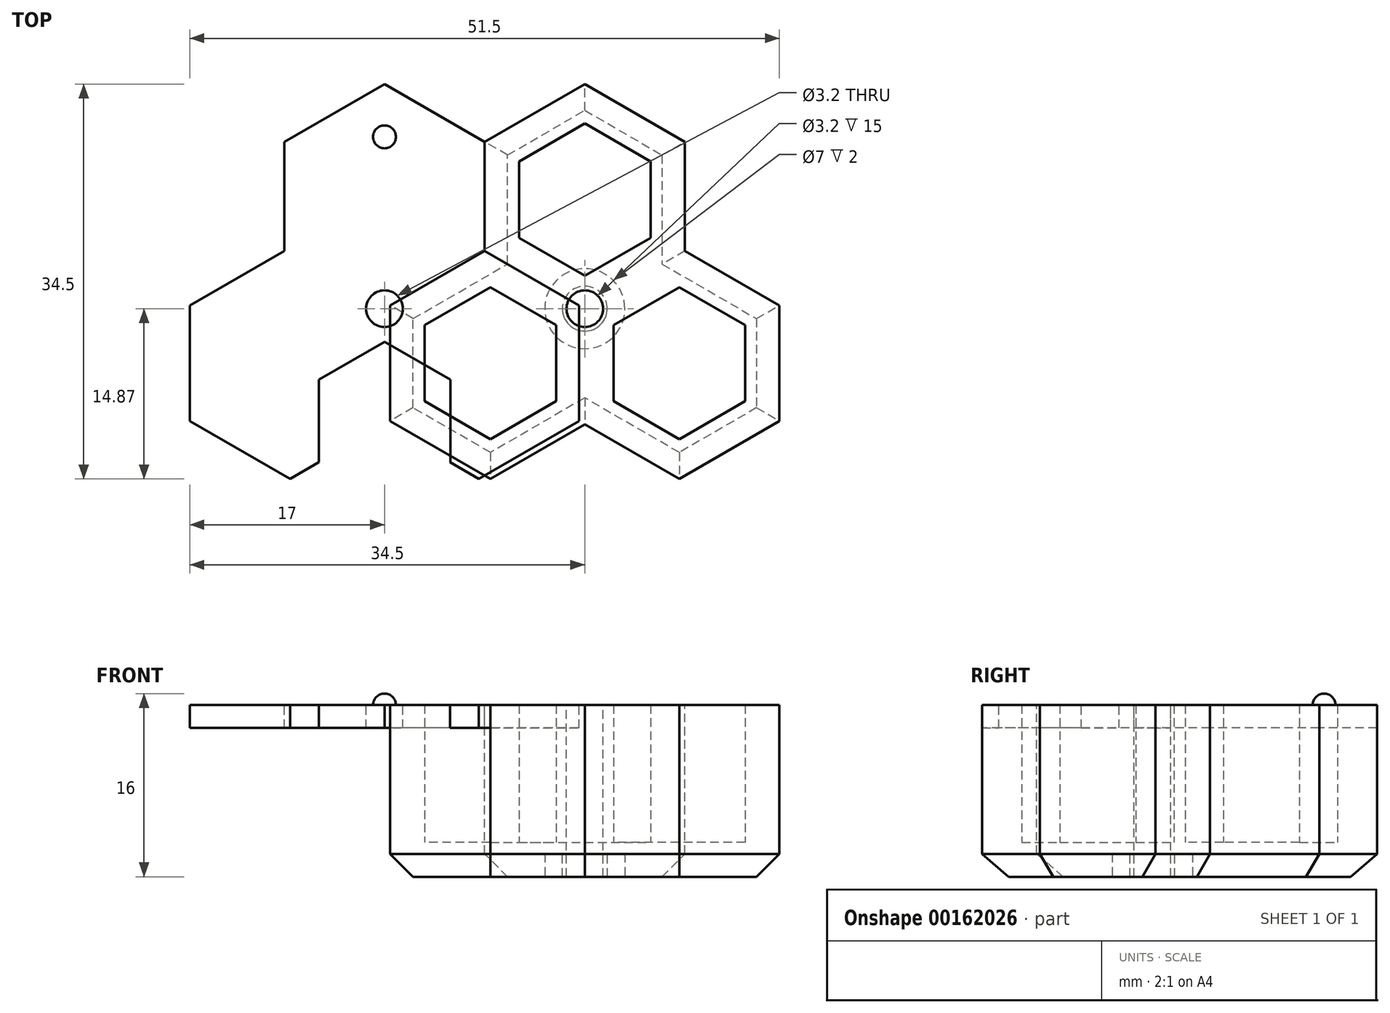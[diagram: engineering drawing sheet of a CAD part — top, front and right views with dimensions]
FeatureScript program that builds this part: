
annotation { "Feature Type Name" : "Feature", "Feature Type Description" : "" }
export const myFeature = defineFeature(function(context is Context, id is Id, definition is map)
    precondition{}
    {
        {
            var Q0;
            Q0=qCreatedBy(makeId("Top.planeOp"),FACE);
            var sketch = newSketch(context, id + "F0", { "sketchPlane" : qUnion([Q0])});
            skLineSegment(sketch, "E0", {"start": v(0, -19.63) * mm, "end": v(0, 19.63) * mm, "construction": true});
            skLineSegment(sketch, "E1.0.MirrorCS", {"start": v(-17, 9.81) * mm, "end": v(17, -9.81) * mm, "construction": true});
            skLineSegment(sketch, "E2.0.MirrorCS", {"start": v(17, 9.81) * mm, "end": v(-17, -9.81) * mm, "construction": true});
            skCircle(sketch, "E3.cCircle", {"center": v(0, 9.53) * mm, "radius": 5.75 * mm, "construction": true});
            skLineSegment(sketch, "E3.0", {"start": v(0, 16.17) * mm, "end": v(5.75, 12.85) * mm});
            skLineSegment(sketch, "E3.1", {"start": v(5.75, 12.85) * mm, "end": v(5.75, 6.2) * mm});
            skLineSegment(sketch, "E3.2", {"start": v(5.75, 6.2) * mm, "end": v(0, 2.89) * mm});
            skLineSegment(sketch, "E3.3", {"start": v(0, 2.89) * mm, "end": v(-5.75, 6.2) * mm});
            skLineSegment(sketch, "E3.4", {"start": v(-5.75, 6.2) * mm, "end": v(-5.75, 12.85) * mm});
            skLineSegment(sketch, "E3.5", {"start": v(-5.75, 12.85) * mm, "end": v(0, 16.17) * mm});
            skCircle(sketch, "E4", {"center": v(0, 0) * mm, "radius": 9.53 * mm, "construction": true});
            skLineSegment(sketch, "E5.1.0", {"start": v(-8.25, -11.4) * mm, "end": v(-14, -8.08) * mm});
            skCircle(sketch, "E5.1.1", {"center": v(-8.25, -4.76) * mm, "radius": 5.75 * mm, "construction": true});
            skLineSegment(sketch, "E5.1.2", {"start": v(-2.5, -8.08) * mm, "end": v(-8.25, -11.4) * mm});
            skLineSegment(sketch, "E5.1.3", {"start": v(-14, -1.44) * mm, "end": v(-8.25, 1.88) * mm});
            skLineSegment(sketch, "E5.1.4", {"start": v(-14, -8.08) * mm, "end": v(-14, -1.44) * mm});
            skLineSegment(sketch, "E5.1.5", {"start": v(-2.5, -1.44) * mm, "end": v(-2.5, -8.08) * mm});
            skLineSegment(sketch, "E5.1.6", {"start": v(-8.25, 1.88) * mm, "end": v(-2.5, -1.44) * mm});
            skLineSegment(sketch, "E5.2.0", {"start": v(14, -1.44) * mm, "end": v(14, -8.08) * mm});
            skCircle(sketch, "E5.2.1", {"center": v(8.25, -4.76) * mm, "radius": 5.75 * mm, "construction": true});
            skLineSegment(sketch, "E5.2.2", {"start": v(8.25, 1.88) * mm, "end": v(14, -1.44) * mm});
            skLineSegment(sketch, "E5.2.3", {"start": v(8.25, -11.4) * mm, "end": v(2.5, -8.08) * mm});
            skLineSegment(sketch, "E5.2.4", {"start": v(14, -8.08) * mm, "end": v(8.25, -11.4) * mm});
            skLineSegment(sketch, "E5.2.5", {"start": v(2.5, -1.44) * mm, "end": v(8.25, 1.88) * mm});
            skLineSegment(sketch, "E5.2.6", {"start": v(2.5, -8.08) * mm, "end": v(2.5, -1.44) * mm});
            skLineSegment(sketch, "E6.0", {"start": v(8.75, 14.58) * mm, "end": v(8.75, 5.05) * mm});
            skLineSegment(sketch, "E6.1", {"start": v(0, 19.63) * mm, "end": v(8.75, 14.58) * mm});
            skLineSegment(sketch, "E6.2", {"start": v(-8.75, 14.58) * mm, "end": v(0, 19.63) * mm});
            skLineSegment(sketch, "E6.3", {"start": v(-8.75, 5.05) * mm, "end": v(-8.75, 14.58) * mm});
            skLineSegment(sketch, "E7.0", {"start": v(-17, 0.29) * mm, "end": v(-8.75, 5.05) * mm});
            skLineSegment(sketch, "E7.1", {"start": v(-17, -9.81) * mm, "end": v(-17, 0.29) * mm});
            skLineSegment(sketch, "E7.2", {"start": v(-8.25, -14.87) * mm, "end": v(-17, -9.81) * mm});
            skLineSegment(sketch, "E7.3", {"start": v(0, -10.1) * mm, "end": v(-8.25, -14.87) * mm});
            skLineSegment(sketch, "E8.0", {"start": v(8.25, -14.87) * mm, "end": v(0, -10.1) * mm});
            skLineSegment(sketch, "E8.1", {"start": v(17, -9.81) * mm, "end": v(8.25, -14.87) * mm});
            skLineSegment(sketch, "E8.2", {"start": v(17, 0.29) * mm, "end": v(17, -9.81) * mm});
            skLineSegment(sketch, "E8.3", {"start": v(8.75, 5.05) * mm, "end": v(17, 0.29) * mm});
            skCircle(sketch, "E9", {"center": v(0, 0) * mm, "radius": 19.63 * mm, "construction": true});
            skCircle(sketch, "E10", {"center": v(0, 0) * mm, "radius": 1.6 * mm});
            skSolve(sketch);
        }
        {
            var Q0;
            Q0=qSketchRegion(id+"F0",true);
            var Q1;
            Q1=makeQuery(id+"F0.imprint","IMPRINT",FACE,{"disambiguationData":[TD([[makeQuery(id+"F0.imprint","IMPRINT",EDGE,{"derivedFrom":sQuery(id+"F0.wireOp",EDGE,"E3.0")}),-1.0]])]});
            var Q2;
            Q2=makeQuery(id+"F0.imprint","IMPRINT",FACE,{"disambiguationData":[TD([[makeQuery(id+"F0.imprint","IMPRINT",EDGE,{"derivedFrom":sQuery(id+"F0.wireOp",EDGE,"E5.1.0")}),-1.0]])]});
            var Q3;
            Q3=makeQuery(id+"F0.imprint","IMPRINT",FACE,{"disambiguationData":[TD([[makeQuery(id+"F0.imprint","IMPRINT",EDGE,{"derivedFrom":sQuery(id+"F0.wireOp",EDGE,"E5.2.0")}),-1.0]])]});
            extrude(context, id + "F1", {"entities" : qUnion([Q0, Q1, Q2, Q3]), "oppositeDirection" : true, "depth" : 3 * mm});
        }
        {
            var Q0;
            Q0=makeQuery(id+"F0.imprint","IMPRINT",FACE,{"disambiguationData":[TD([[makeQuery(id+"F0.imprint","IMPRINT",EDGE,{"derivedFrom":sQuery(id+"F0.wireOp",EDGE,"E3.0")}),1.0]])]});
            extrude(context, id + "F2", {"entities" : qUnion([Q0]), "operationType" : NewBodyOperationType.ADD, "depth" : 12 * mm});
        }
        {
            var Q0;
            Q0=makeQuery(id+"F1.opExtrude","CAP_FACE",FACE,{"disambiguationData":[OSD([sQuery(id+"F0.wireOp",EDGE,"E6.0"),sQuery(id+"F0.wireOp",EDGE,"E6.1"),sQuery(id+"F0.wireOp",EDGE,"E6.2"),sQuery(id+"F0.wireOp",EDGE,"E6.3"),sQuery(id+"F0.wireOp",EDGE,"E7.0"),sQuery(id+"F0.wireOp",EDGE,"E7.1"),sQuery(id+"F0.wireOp",EDGE,"E7.2"),sQuery(id+"F0.wireOp",EDGE,"E7.3"),sQuery(id+"F0.wireOp",EDGE,"E8.0"),sQuery(id+"F0.wireOp",EDGE,"E8.1"),sQuery(id+"F0.wireOp",EDGE,"E8.2"),sQuery(id+"F0.wireOp",EDGE,"E8.3"),sQuery(id+"F0.wireOp",EDGE,"E10")])],"isStart":false});
            var sketch = newSketch(context, id + "F3", { "sketchPlane" : qUnion([Q0])});
            skCircle(sketch, "E11", {"center": v(0, 0) * mm, "radius": 3.5 * mm});
            skSolve(sketch);
        }
        {
            var Q0;
            Q0=qSketchRegion(id+"F3",true);
            extrude(context, id + "F4", {"entities" : qUnion([Q0]), "operationType" : NewBodyOperationType.REMOVE, "oppositeDirection" : true, "depth" : 2 * mm});
        }
        {
            var Q0;
            Q0=makeQuery(id+"F1.opExtrude","CAP_EDGE",EDGE,{"disambiguationData":[OSD([sQuery(id+"F0.wireOp",EDGE,"E7.2")])],"isStart":false});
            var Q1;
            Q1=makeQuery(id+"F1.opExtrude","CAP_EDGE",EDGE,{"disambiguationData":[OSD([sQuery(id+"F0.wireOp",EDGE,"E7.3")])],"isStart":false});
            var Q2;
            Q2=makeQuery(id+"F1.opExtrude","CAP_EDGE",EDGE,{"disambiguationData":[OSD([sQuery(id+"F0.wireOp",EDGE,"E8.0")])],"isStart":false});
            var Q3;
            Q3=makeQuery(id+"F1.opExtrude","CAP_EDGE",EDGE,{"disambiguationData":[OSD([sQuery(id+"F0.wireOp",EDGE,"E8.1")])],"isStart":false});
            var Q4;
            Q4=makeQuery(id+"F1.opExtrude","CAP_EDGE",EDGE,{"disambiguationData":[OSD([sQuery(id+"F0.wireOp",EDGE,"E8.2")])],"isStart":false});
            var Q5;
            Q5=makeQuery(id+"F1.opExtrude","CAP_EDGE",EDGE,{"disambiguationData":[OSD([sQuery(id+"F0.wireOp",EDGE,"E8.3")])],"isStart":false});
            var Q6;
            Q6=makeQuery(id+"F1.opExtrude","CAP_EDGE",EDGE,{"disambiguationData":[OSD([sQuery(id+"F0.wireOp",EDGE,"E6.0")])],"isStart":false});
            var Q7;
            Q7=makeQuery(id+"F1.opExtrude","CAP_EDGE",EDGE,{"disambiguationData":[OSD([sQuery(id+"F0.wireOp",EDGE,"E6.1")])],"isStart":false});
            var Q8;
            Q8=makeQuery(id+"F1.opExtrude","CAP_EDGE",EDGE,{"disambiguationData":[OSD([sQuery(id+"F0.wireOp",EDGE,"E6.2")])],"isStart":false});
            var Q9;
            Q9=makeQuery(id+"F1.opExtrude","CAP_EDGE",EDGE,{"disambiguationData":[OSD([sQuery(id+"F0.wireOp",EDGE,"E6.3")])],"isStart":false});
            var Q10;
            Q10=makeQuery(id+"F1.opExtrude","CAP_EDGE",EDGE,{"disambiguationData":[OSD([sQuery(id+"F0.wireOp",EDGE,"E7.0")])],"isStart":false});
            var Q11;
            Q11=makeQuery(id+"F1.opExtrude","CAP_EDGE",EDGE,{"disambiguationData":[OSD([sQuery(id+"F0.wireOp",EDGE,"E7.1")])],"isStart":false});
            chamfer(context, id + "F5", {"entities" : qUnion([Q0, Q1, Q2, Q3, Q4, Q5, Q6, Q7, Q8, Q9, Q10, Q11]), "width" : 2 * mm, "tangentPropagation" : true});
        }
        {
            var Q0;
            Q0=makeQuery(id+"F4.boolean.opBoolean","COPY",FACE,{"derivedFrom":makeQuery(id+"F4.opExtrude","CAP_FACE",FACE,{"disambiguationData":[OSD([sQuery(id+"F3.wireOp",EDGE,"E11")])],"isStart":false})});
            var sketch = newSketch(context, id + "F6", { "sketchPlane" : qUnion([Q0])});
            skCircle(sketch, "E12", {"center": v(0, 0) * mm, "radius": 1.6 * mm});
            skCircle(sketch, "E13.0", {"center": v(0, 0) * mm, "radius": 1.96 * mm});
            skSolve(sketch);
        }
        {
            var Q0;
            Q0=qSketchRegion(id+"F6",true);
            var Q1;
            Q1=makeQuery(id+"F1.opExtrude","CAP_FACE",FACE,{"disambiguationData":[OSD([sQuery(id+"F0.wireOp",EDGE,"E6.0"),sQuery(id+"F0.wireOp",EDGE,"E6.1"),sQuery(id+"F0.wireOp",EDGE,"E6.2"),sQuery(id+"F0.wireOp",EDGE,"E6.3"),sQuery(id+"F0.wireOp",EDGE,"E7.0"),sQuery(id+"F0.wireOp",EDGE,"E7.1"),sQuery(id+"F0.wireOp",EDGE,"E7.2"),sQuery(id+"F0.wireOp",EDGE,"E7.3"),sQuery(id+"F0.wireOp",EDGE,"E8.0"),sQuery(id+"F0.wireOp",EDGE,"E8.1"),sQuery(id+"F0.wireOp",EDGE,"E8.2"),sQuery(id+"F0.wireOp",EDGE,"E8.3"),sQuery(id+"F0.wireOp",EDGE,"E10")])],"isStart":false});
            extrude(context, id + "F7", {"entities" : qUnion([Q0]), "operationType" : NewBodyOperationType.ADD, "endBound" : BoundingType.UP_TO_SURFACE, "endBoundEntityFace" : qUnion([Q1]), "depth" : 25 * mm});
        }
        {
            var Q0;
            Q0=makeQuery(id+"F2.opExtrude","CAP_FACE",FACE,{"disambiguationData":[OSD([sQuery(id+"F0.wireOp",EDGE,"E3.0"),sQuery(id+"F0.wireOp",EDGE,"E3.1"),sQuery(id+"F0.wireOp",EDGE,"E3.2"),sQuery(id+"F0.wireOp",EDGE,"E3.3"),sQuery(id+"F0.wireOp",EDGE,"E3.4"),sQuery(id+"F0.wireOp",EDGE,"E3.5"),sQuery(id+"F0.wireOp",EDGE,"E5.1.0"),sQuery(id+"F0.wireOp",EDGE,"E5.1.2"),sQuery(id+"F0.wireOp",EDGE,"E5.1.3"),sQuery(id+"F0.wireOp",EDGE,"E5.1.4"),sQuery(id+"F0.wireOp",EDGE,"E5.1.5"),sQuery(id+"F0.wireOp",EDGE,"E5.1.6"),sQuery(id+"F0.wireOp",EDGE,"E5.2.0"),sQuery(id+"F0.wireOp",EDGE,"E5.2.2"),sQuery(id+"F0.wireOp",EDGE,"E5.2.3"),sQuery(id+"F0.wireOp",EDGE,"E5.2.4"),sQuery(id+"F0.wireOp",EDGE,"E5.2.5"),sQuery(id+"F0.wireOp",EDGE,"E5.2.6"),sQuery(id+"F0.wireOp",EDGE,"E6.0"),sQuery(id+"F0.wireOp",EDGE,"E6.1"),sQuery(id+"F0.wireOp",EDGE,"E6.2"),sQuery(id+"F0.wireOp",EDGE,"E6.3"),sQuery(id+"F0.wireOp",EDGE,"E7.0"),sQuery(id+"F0.wireOp",EDGE,"E7.1"),sQuery(id+"F0.wireOp",EDGE,"E7.2"),sQuery(id+"F0.wireOp",EDGE,"E7.3"),sQuery(id+"F0.wireOp",EDGE,"E8.0"),sQuery(id+"F0.wireOp",EDGE,"E8.1"),sQuery(id+"F0.wireOp",EDGE,"E8.2"),sQuery(id+"F0.wireOp",EDGE,"E8.3"),sQuery(id+"F0.wireOp",EDGE,"E10")])],"isStart":false});
            var sketch = newSketch(context, id + "F8", { "sketchPlane" : qUnion([Q0])});
            skLineSegment(sketch, "E14.0", {"start": v(17, 0.29) * mm, "end": v(17, -9.81) * mm});
            skLineSegment(sketch, "E15.0", {"start": v(8.75, 5.05) * mm, "end": v(17, 0.29) * mm});
            skLineSegment(sketch, "E16.0", {"start": v(8.75, 14.58) * mm, "end": v(8.75, 5.05) * mm});
            skLineSegment(sketch, "E17.0", {"start": v(0, 19.63) * mm, "end": v(8.75, 14.58) * mm});
            skLineSegment(sketch, "E18.0", {"start": v(-8.75, 14.58) * mm, "end": v(0, 19.63) * mm});
            skLineSegment(sketch, "E19.0", {"start": v(-8.75, 5.05) * mm, "end": v(-8.75, 14.58) * mm});
            skLineSegment(sketch, "E20.0", {"start": v(-17, 0.29) * mm, "end": v(-8.75, 5.05) * mm});
            skLineSegment(sketch, "E21.0", {"start": v(-17, -9.81) * mm, "end": v(-17, 0.29) * mm});
            skLineSegment(sketch, "E22.0", {"start": v(-8.25, -14.87) * mm, "end": v(-17, -9.81) * mm});
            skLineSegment(sketch, "E23.0", {"start": v(0, -10.1) * mm, "end": v(-8.25, -14.87) * mm});
            skLineSegment(sketch, "E24.0", {"start": v(8.25, -14.87) * mm, "end": v(0, -10.1) * mm});
            skLineSegment(sketch, "E25.0", {"start": v(17, -9.81) * mm, "end": v(8.25, -14.87) * mm});
            skCircle(sketch, "E26.0", {"center": v(0, 0) * mm, "radius": 1.6 * mm});
            skLineSegment(sketch, "E27", {"start": v(15.07, 0) * mm, "end": v(-15.75, 0) * mm, "construction": true});
            skLineSegment(sketch, "E28.0.MirrorCS", {"start": v(-5.75, -6.2) * mm, "end": v(0, -2.89) * mm});
            skLineSegment(sketch, "E28.2.MirrorCS", {"start": v(0, -2.89) * mm, "end": v(5.75, -6.2) * mm});
            skLineSegment(sketch, "E28.3.MirrorCS", {"start": v(-5.75, -13.42) * mm, "end": v(-5.75, -6.2) * mm});
            skLineSegment(sketch, "E28.5.MirrorCS", {"start": v(5.75, -6.2) * mm, "end": v(5.75, -13.42) * mm});
            skLineSegment(sketch, "E29", {"start": v(-5.75, -13.42) * mm, "end": v(5.75, -13.42) * mm});
            skSolve(sketch);
        }
        {
            var Q0;
            {var subQ7=makeQuery(id+"F2.opExtrude","CAP_EDGE",EDGE,{"disambiguationData":[OSD([sQuery(id+"F0.wireOp",EDGE,"E5.1.0")])],"isStart":false});Q0=makeQuery(id+"F8.imprint","IMPRINT",FACE,{"disambiguationData":[TD([[makeQuery(id+"F8.imprint","IMPRINT",EDGE,{"derivedFrom":subQ7}),-1.0]])]});}
            var Q1;
            Q1=makeQuery(id+"F8.imprint","IMPRINT",FACE,{"disambiguationData":[TD([[makeQuery(id+"F8.imprint","IMPRINT",EDGE,{"derivedFrom":makeQuery(id+"F2.opExtrude","CAP_EDGE",EDGE,{"disambiguationData":[OSD([sQuery(id+"F0.wireOp",EDGE,"E5.2.0")])],"isStart":false})}),-1.0]])]});
            var Q2;
            Q2=makeQuery(id+"F8.imprint","IMPRINT",FACE,{"disambiguationData":[TD([[makeQuery(id+"F8.imprint","IMPRINT",EDGE,{"derivedFrom":sQuery(id+"F8.wireOp",EDGE,"E14.0")}),-1.0]])]});
            var Q3;
            Q3=makeQuery(id+"F8.imprint","IMPRINT",FACE,{"disambiguationData":[TD([[makeQuery(id+"F8.imprint","IMPRINT",EDGE,{"derivedFrom":makeQuery(id+"F2.opExtrude","CAP_EDGE",EDGE,{"disambiguationData":[OSD([sQuery(id+"F0.wireOp",EDGE,"E3.0")])],"isStart":false})}),-1.0]])]});
            extrude(context, id + "F9", {"entities" : qUnion([Q0, Q1, Q2, Q3]), "depth" : 2 * mm});
        }
        {
            var Q0;
            Q0=makeQuery(id+"F8.imprint","IMPRINT",FACE,{"disambiguationData":[TD([[makeQuery(id+"F8.imprint","IMPRINT",EDGE,{"derivedFrom":sQuery(id+"F8.wireOp",EDGE,"E14.0")}),-1.0]])]});
            var sketch = newSketch(context, id + "F10", { "sketchPlane" : qUnion([Q0])});
            skLineSegment(sketch, "E30", {"start": v(1, 15.01) * mm, "end": v(-1, 15.01) * mm});
            skArc(sketch, "E31", {"start": v(1, 15.01) * mm, "mid": v(0, 16.01) * mm, "end": v(-1, 15.01) * mm, "construction": true});
            skArc(sketch, "E32", {"start": v(-1, 15.01) * mm, "mid": v(0, 14.01) * mm, "end": v(1, 15.01) * mm});
            skSolve(sketch);
        }
        {
            var Q0;
            Q0=qSketchRegion(id+"F10",true);
            var Q1;
            Q1=sQuery(id+"F10.wireOp",EDGE,"E30");
            revolve(context, id + "F11", {"operationType" : NewBodyOperationType.ADD, "entities" : qUnion([Q0]), "axis" : qUnion([Q1]), "revolveType" : RevolveType.ONE_DIRECTION, "oppositeDirection" : true, "angle" : 180 * degree});
        }
        {
            var Q0;
            Q0=makeQuery(id+"F9.opExtrude","SWEPT_BODY",BODY,{"disambiguationData":[OSD([sQuery(id+"F8.wireOp",EDGE,"E14.0"),sQuery(id+"F8.wireOp",EDGE,"E15.0"),sQuery(id+"F8.wireOp",EDGE,"E16.0"),sQuery(id+"F8.wireOp",EDGE,"E17.0"),sQuery(id+"F8.wireOp",EDGE,"E18.0"),sQuery(id+"F8.wireOp",EDGE,"E19.0"),sQuery(id+"F8.wireOp",EDGE,"E20.0"),sQuery(id+"F8.wireOp",EDGE,"E21.0"),sQuery(id+"F8.wireOp",EDGE,"E22.0"),sQuery(id+"F8.wireOp",EDGE,"E23.0"),sQuery(id+"F8.wireOp",EDGE,"E24.0"),sQuery(id+"F8.wireOp",EDGE,"E25.0"),sQuery(id+"F8.wireOp",EDGE,"E26.0"),sQuery(id+"F8.wireOp",EDGE,"E28.0.MirrorCS"),sQuery(id+"F8.wireOp",EDGE,"E28.2.MirrorCS"),sQuery(id+"F8.wireOp",EDGE,"E28.3.MirrorCS"),sQuery(id+"F8.wireOp",EDGE,"E28.5.MirrorCS")])]});
            var Q1;
            Q1=makeQuery(id+"F9.opExtrude","CAP_EDGE",EDGE,{"disambiguationData":[OSD([sQuery(id+"F8.wireOp",EDGE,"E19.0")])],"isStart":true});
            transform(context, id + "F12", {"entities" : qUnion([Q0]), "transformType" : TransformType.ROTATION, "transformAxis" : qUnion([Q1]), "angle" : 180 * degree, "makeCopy" : false});
        }
    });
